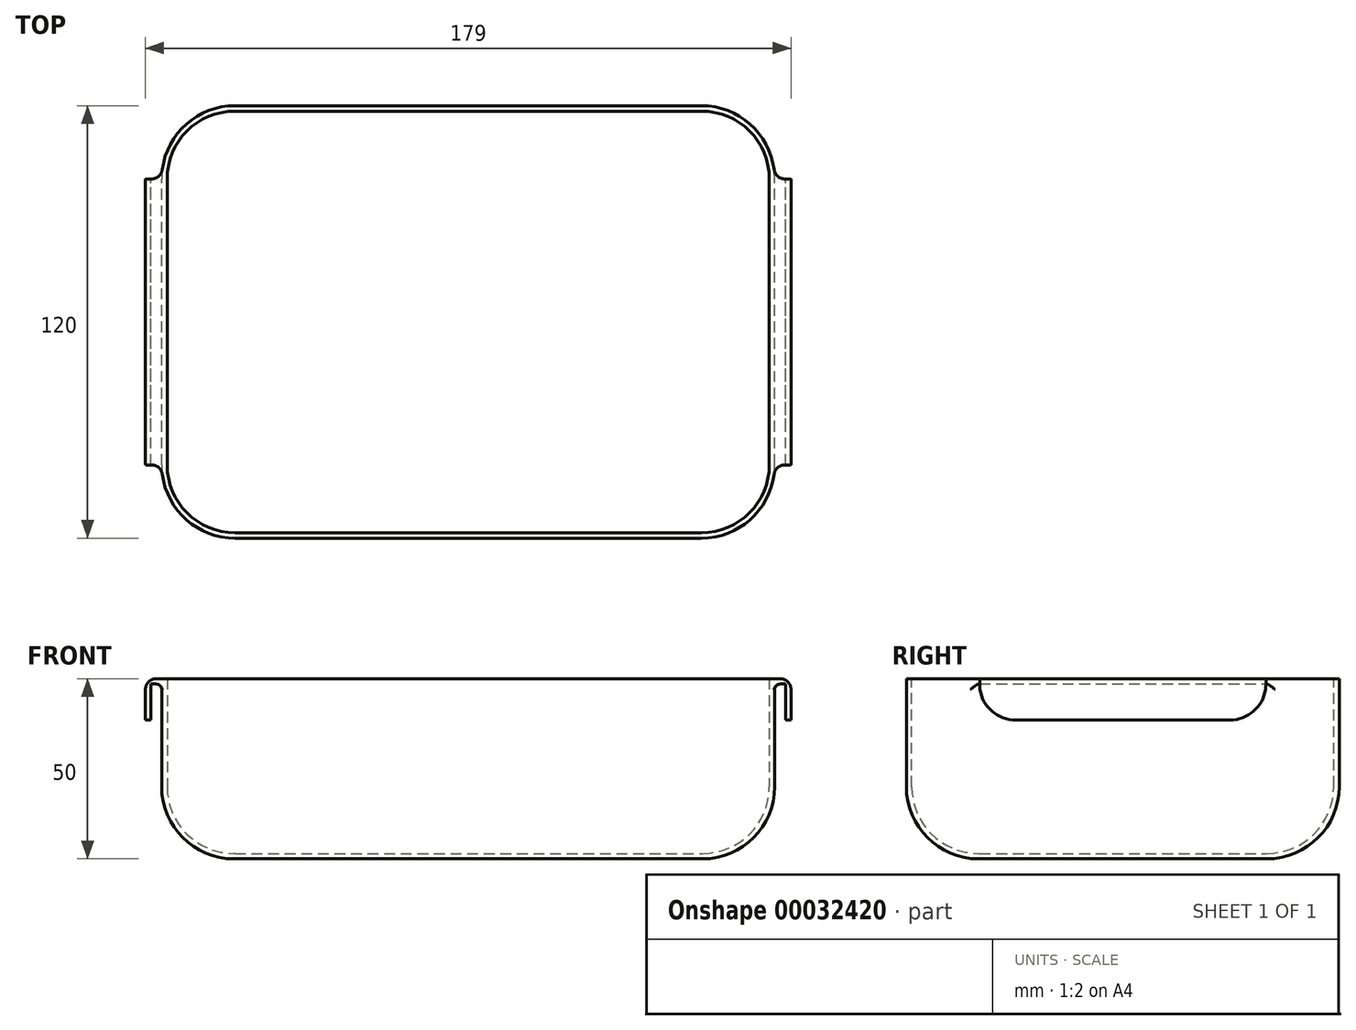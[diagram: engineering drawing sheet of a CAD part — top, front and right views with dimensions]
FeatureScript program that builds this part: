
annotation { "Feature Type Name" : "Feature", "Feature Type Description" : "" }
export const myFeature = defineFeature(function(context is Context, id is Id, definition is map)
    precondition{}
    {
        {
            var Q0;
            Q0=qCreatedBy(makeId("Top.planeOp"),FACE);
            var sketch = newSketch(context, id + "F0", { "sketchPlane" : qUnion([Q0])});
            skLineSegment(sketch, "E0.bottom", {"start": v(20.32, 0) * mm, "end": v(149.68, 0) * mm});
            skLineSegment(sketch, "E0.top", {"start": v(20.32, 120) * mm, "end": v(149.68, 120) * mm});
            skLineSegment(sketch, "E0.left", {"start": v(0, 20.32) * mm, "end": v(0, 99.68) * mm});
            skLineSegment(sketch, "E0.right", {"start": v(170, 20.32) * mm, "end": v(170, 99.68) * mm});
            skPoint(sketch, "E1.visualSharp", {"position": v(0, 120) * mm});
            skArc(sketch, "E1.filletArc", {"start": v(20.32, 120) * mm, "mid": v(5.95, 114.05) * mm, "end": v(0, 99.68) * mm});
            skPoint(sketch, "E2.visualSharp", {"position": v(170, 120) * mm});
            skArc(sketch, "E2.filletArc", {"start": v(170, 99.68) * mm, "mid": v(164.05, 114.05) * mm, "end": v(149.68, 120) * mm});
            skPoint(sketch, "E3.visualSharp", {"position": v(170, 0) * mm});
            skArc(sketch, "E3.filletArc", {"start": v(149.68, 0) * mm, "mid": v(164.05, 5.95) * mm, "end": v(170, 20.32) * mm});
            skPoint(sketch, "E4.visualSharp", {"position": v(0, 0) * mm});
            skArc(sketch, "E4.filletArc", {"start": v(0, 20.32) * mm, "mid": v(5.95, 5.95) * mm, "end": v(20.32, 0) * mm});
            skSolve(sketch);
        }
        {
            var Q0;
            Q0=makeQuery(id+"F0.imprint","IMPRINT",FACE,{"disambiguationData":[TD([[makeQuery(id+"F0.imprint","IMPRINT",EDGE,{"derivedFrom":sQuery(id+"F0.wireOp",EDGE,"E0.bottom")}),1.0]])]});
            extrude(context, id + "F1", {"entities" : qUnion([Q0]), "depth" : 50 * mm});
        }
        {
            var Q0;
            Q0=makeQuery(id+"F1.opExtrude","CAP_FACE",FACE,{"disambiguationData":[OSD([sQuery(id+"F0.wireOp",EDGE,"E0.bottom"),sQuery(id+"F0.wireOp",EDGE,"E0.top"),sQuery(id+"F0.wireOp",EDGE,"E0.left"),sQuery(id+"F0.wireOp",EDGE,"E0.right"),sQuery(id+"F0.wireOp",EDGE,"E1.filletArc"),sQuery(id+"F0.wireOp",EDGE,"E2.filletArc"),sQuery(id+"F0.wireOp",EDGE,"E3.filletArc"),sQuery(id+"F0.wireOp",EDGE,"E4.filletArc")])],"isStart":true});
            fillet(context, id + "F2", {"entities" : qUnion([Q0]), "radius" : 20 * mm, "tangentPropagation" : true, "allowEdgeOverflow" : false});
        }
        {
            var Q0;
            Q0=makeQuery(id+"F1.opExtrude","CAP_FACE",FACE,{"disambiguationData":[OSD([sQuery(id+"F0.wireOp",EDGE,"E0.bottom"),sQuery(id+"F0.wireOp",EDGE,"E0.top"),sQuery(id+"F0.wireOp",EDGE,"E0.left"),sQuery(id+"F0.wireOp",EDGE,"E0.right"),sQuery(id+"F0.wireOp",EDGE,"E1.filletArc"),sQuery(id+"F0.wireOp",EDGE,"E2.filletArc"),sQuery(id+"F0.wireOp",EDGE,"E3.filletArc"),sQuery(id+"F0.wireOp",EDGE,"E4.filletArc")])],"isStart":false});
            var sketch = newSketch(context, id + "F3", { "sketchPlane" : qUnion([Q0])});
            skLineSegment(sketch, "E5.bottom", {"start": v(0, 99.68) * mm, "end": v(-4.5, 99.68) * mm});
            skLineSegment(sketch, "E5.top", {"start": v(0, 20.32) * mm, "end": v(-4.5, 20.32) * mm});
            skLineSegment(sketch, "E5.right", {"start": v(-4.5, 99.68) * mm, "end": v(-4.5, 20.32) * mm});
            skLineSegment(sketch, "E6.bottom", {"start": v(170, 99.68) * mm, "end": v(174.5, 99.68) * mm});
            skLineSegment(sketch, "E6.top", {"start": v(170, 20.32) * mm, "end": v(174.5, 20.32) * mm});
            skLineSegment(sketch, "E6.right", {"start": v(174.5, 99.68) * mm, "end": v(174.5, 20.32) * mm});
            skArc(sketch, "E7.0", {"start": v(20.32, 120) * mm, "mid": v(5.95, 114.05) * mm, "end": v(0, 99.68) * mm});
            skLineSegment(sketch, "E7.1", {"start": v(20.32, 120) * mm, "end": v(149.68, 120) * mm});
            skArc(sketch, "E7.2", {"start": v(170, 99.68) * mm, "mid": v(164.05, 114.05) * mm, "end": v(149.68, 120) * mm});
            skArc(sketch, "E7.3", {"start": v(149.68, 0) * mm, "mid": v(164.05, 5.95) * mm, "end": v(170, 20.32) * mm});
            skLineSegment(sketch, "E7.4", {"start": v(20.32, 0) * mm, "end": v(149.68, 0) * mm});
            skArc(sketch, "E7.5", {"start": v(0, 20.32) * mm, "mid": v(5.95, 5.95) * mm, "end": v(20.32, 0) * mm});
            skSolve(sketch);
        }
        {
            var Q0;
            Q0 = qSketchRegion(id + "F3", true);
            extrude(context, id + "F4", {"entities" : qUnion([Q0]), "operationType" : NewBodyOperationType.ADD, "oppositeDirection" : true, "depth" : 1.5 * mm});
        }
        {
            var Q0;
            Q0=makeQuery(id+"F4.boolean.opBoolean","MERGE",FACE,{"derivedFrom":[makeQuery(id+"F1.opExtrude","CAP_FACE",FACE,{"disambiguationData":[OSD([sQuery(id+"F0.wireOp",EDGE,"E0.bottom"),sQuery(id+"F0.wireOp",EDGE,"E0.top"),sQuery(id+"F0.wireOp",EDGE,"E0.left"),sQuery(id+"F0.wireOp",EDGE,"E0.right"),sQuery(id+"F0.wireOp",EDGE,"E1.filletArc"),sQuery(id+"F0.wireOp",EDGE,"E2.filletArc"),sQuery(id+"F0.wireOp",EDGE,"E3.filletArc"),sQuery(id+"F0.wireOp",EDGE,"E4.filletArc")])],"isStart":false}),makeQuery(id+"F4.opExtrude","CAP_FACE",FACE,{"disambiguationData":[OSD([sQuery(id+"F3.wireOp",EDGE,"E5.bottom"),sQuery(id+"F3.wireOp",EDGE,"E5.top"),sQuery(id+"F3.wireOp",EDGE,"E5.right"),sQuery(id+"F3.wireOp",EDGE,"E6.bottom"),sQuery(id+"F3.wireOp",EDGE,"E6.top"),sQuery(id+"F3.wireOp",EDGE,"E6.right"),sQuery(id+"F3.wireOp",EDGE,"E7.0"),sQuery(id+"F3.wireOp",EDGE,"E7.1"),sQuery(id+"F3.wireOp",EDGE,"E7.2"),sQuery(id+"F3.wireOp",EDGE,"E7.3"),sQuery(id+"F3.wireOp",EDGE,"E7.4"),sQuery(id+"F3.wireOp",EDGE,"E7.5")])],"isStart":true})]});
            shell(context, id + "F5", {"entities" : qUnion([Q0]), "thickness" : 1.5 * mm});
        }
        {
            var Q0;
            {var subQ0=sQuery(id+"F3.wireOp",EDGE,"E6.bottom");var subQ1=sQuery(id+"F3.wireOp",EDGE,"E6.top");var subQ2=sQuery(id+"F3.wireOp",EDGE,"E6.right");Q0=makeQuery(id+"F4.boolean.opBoolean","SPLIT",FACE,{"disambiguationData":[TD([makeQuery(id+"F1.opExtrude","SWEPT_FACE",FACE,{"disambiguationData":[OSD([sQuery(id+"F0.wireOp",EDGE,"E0.right")])]})])],"derivedFrom":makeQuery(id+"F4.opExtrude","CAP_FACE",FACE,{"disambiguationData":[OSD([sQuery(id+"F3.wireOp",EDGE,"E5.bottom"),sQuery(id+"F3.wireOp",EDGE,"E5.top"),sQuery(id+"F3.wireOp",EDGE,"E5.right"),subQ0,subQ1,subQ2,sQuery(id+"F3.wireOp",EDGE,"E7.0"),sQuery(id+"F3.wireOp",EDGE,"E7.1"),sQuery(id+"F3.wireOp",EDGE,"E7.2"),sQuery(id+"F3.wireOp",EDGE,"E7.3"),sQuery(id+"F3.wireOp",EDGE,"E7.4"),sQuery(id+"F3.wireOp",EDGE,"E7.5")])],"isStart":false})});}
            var sketch = newSketch(context, id + "F6", { "sketchPlane" : qUnion([Q0])});
            skLineSegment(sketch, "E8.bottom", {"start": v(174.5, -20.32) * mm, "end": v(173, -20.32) * mm});
            skLineSegment(sketch, "E8.top", {"start": v(174.5, -99.68) * mm, "end": v(173, -99.68) * mm});
            skLineSegment(sketch, "E8.left", {"start": v(174.5, -20.32) * mm, "end": v(174.5, -99.68) * mm});
            skLineSegment(sketch, "E8.right", {"start": v(173, -20.32) * mm, "end": v(173, -99.68) * mm});
            skSolve(sketch);
        }
        {
            var Q0;
            Q0 = qSketchRegion(id + "F6", true);
            extrude(context, id + "F7", {"entities" : qUnion([Q0]), "operationType" : NewBodyOperationType.ADD, "depth" : 10 * mm});
        }
        {
            var Q0;
            {var subQ0=sQuery(id+"F3.wireOp",EDGE,"E5.bottom");var subQ1=sQuery(id+"F3.wireOp",EDGE,"E5.top");var subQ2=sQuery(id+"F3.wireOp",EDGE,"E5.right");Q0=makeQuery(id+"F4.boolean.opBoolean","SPLIT",FACE,{"disambiguationData":[TD([makeQuery(id+"F1.opExtrude","SWEPT_FACE",FACE,{"disambiguationData":[OSD([sQuery(id+"F0.wireOp",EDGE,"E0.left")])]})])],"derivedFrom":makeQuery(id+"F4.opExtrude","CAP_FACE",FACE,{"disambiguationData":[OSD([subQ0,subQ1,subQ2,sQuery(id+"F3.wireOp",EDGE,"E6.bottom"),sQuery(id+"F3.wireOp",EDGE,"E6.top"),sQuery(id+"F3.wireOp",EDGE,"E6.right"),sQuery(id+"F3.wireOp",EDGE,"E7.0"),sQuery(id+"F3.wireOp",EDGE,"E7.1"),sQuery(id+"F3.wireOp",EDGE,"E7.2"),sQuery(id+"F3.wireOp",EDGE,"E7.3"),sQuery(id+"F3.wireOp",EDGE,"E7.4"),sQuery(id+"F3.wireOp",EDGE,"E7.5")])],"isStart":false})});}
            var sketch = newSketch(context, id + "F8", { "sketchPlane" : qUnion([Q0])});
            skLineSegment(sketch, "E9.bottom", {"start": v(-4.5, -20.32) * mm, "end": v(-3, -20.32) * mm});
            skLineSegment(sketch, "E9.top", {"start": v(-4.5, -99.68) * mm, "end": v(-3, -99.68) * mm});
            skLineSegment(sketch, "E9.left", {"start": v(-4.5, -20.32) * mm, "end": v(-4.5, -99.68) * mm});
            skLineSegment(sketch, "E9.right", {"start": v(-3, -20.32) * mm, "end": v(-3, -99.68) * mm});
            skSolve(sketch);
        }
        {
            var Q0;
            Q0 = qSketchRegion(id + "F8", true);
            extrude(context, id + "F9", {"entities" : qUnion([Q0]), "operationType" : NewBodyOperationType.ADD, "depth" : 10 * mm});
        }
        {
            var Q0;
            {var subQ0=sQuery(id+"F0.wireOp",EDGE,"E0.right");Q0=makeQuery(id+"F4.boolean.opBoolean","MERGE",EDGE,{"derivedFrom":[makeQuery(id+"F1.opExtrude","SWEPT_EDGE",EDGE,{"disambiguationData":[OSD([subQ0,sQuery(id+"F0.wireOp",EDGE,"E3.filletArc")])]}),makeQuery(id+"F4.opExtrude","SWEPT_EDGE",EDGE,{"disambiguationData":[OSD([subQ0,sQuery(id+"F3.wireOp",EDGE,"E6.top"),sQuery(id+"F3.wireOp",EDGE,"E7.3")])]})]});}
            var Q1;
            {var subQ0=sQuery(id+"F0.wireOp",EDGE,"E0.right");Q1=makeQuery(id+"F4.boolean.opBoolean","MERGE",EDGE,{"derivedFrom":[makeQuery(id+"F1.opExtrude","SWEPT_EDGE",EDGE,{"disambiguationData":[OSD([subQ0,sQuery(id+"F0.wireOp",EDGE,"E2.filletArc")])]}),makeQuery(id+"F4.opExtrude","SWEPT_EDGE",EDGE,{"disambiguationData":[OSD([subQ0,sQuery(id+"F3.wireOp",EDGE,"E6.bottom"),sQuery(id+"F3.wireOp",EDGE,"E7.2")])]})]});}
            var Q2;
            {var subQ0=sQuery(id+"F0.wireOp",EDGE,"E0.left");Q2=makeQuery(id+"F4.boolean.opBoolean","MERGE",EDGE,{"derivedFrom":[makeQuery(id+"F1.opExtrude","SWEPT_EDGE",EDGE,{"disambiguationData":[OSD([subQ0,sQuery(id+"F0.wireOp",EDGE,"E1.filletArc")])]}),makeQuery(id+"F4.opExtrude","SWEPT_EDGE",EDGE,{"disambiguationData":[OSD([subQ0,sQuery(id+"F3.wireOp",EDGE,"E5.bottom"),sQuery(id+"F3.wireOp",EDGE,"E7.0")])]})]});}
            var Q3;
            {var subQ0=sQuery(id+"F0.wireOp",EDGE,"E0.left");Q3=makeQuery(id+"F4.boolean.opBoolean","MERGE",EDGE,{"derivedFrom":[makeQuery(id+"F1.opExtrude","SWEPT_EDGE",EDGE,{"disambiguationData":[OSD([subQ0,sQuery(id+"F0.wireOp",EDGE,"E4.filletArc")])]}),makeQuery(id+"F4.opExtrude","SWEPT_EDGE",EDGE,{"disambiguationData":[OSD([subQ0,sQuery(id+"F3.wireOp",EDGE,"E5.top"),sQuery(id+"F3.wireOp",EDGE,"E7.5")])]})]});}
            fillet(context, id + "F10", {"entities" : qUnion([Q0, Q1, Q2, Q3]), "radius" : 2.96 * mm, "tangentPropagation" : true, "allowEdgeOverflow" : false});
        }
        {
            var Q0;
            Q0=makeQuery(id+"F9.opExtrude","CAP_EDGE",EDGE,{"disambiguationData":[OSD([sQuery(id+"F8.wireOp",EDGE,"E9.right")])],"isStart":true});
            var Q1;
            Q1=makeQuery(id+"F4.boolean.opBoolean","INTERSECT",EDGE,{"derivedFrom":[makeQuery(id+"F1.opExtrude","SWEPT_FACE",FACE,{"disambiguationData":[OSD([sQuery(id+"F0.wireOp",EDGE,"E0.left")])]}),makeQuery(id+"F4.opExtrude","CAP_FACE",FACE,{"disambiguationData":[OSD([sQuery(id+"F3.wireOp",EDGE,"E5.bottom"),sQuery(id+"F3.wireOp",EDGE,"E5.top"),sQuery(id+"F3.wireOp",EDGE,"E5.right"),sQuery(id+"F3.wireOp",EDGE,"E6.bottom"),sQuery(id+"F3.wireOp",EDGE,"E6.top"),sQuery(id+"F3.wireOp",EDGE,"E6.right"),sQuery(id+"F3.wireOp",EDGE,"E7.0"),sQuery(id+"F3.wireOp",EDGE,"E7.1"),sQuery(id+"F3.wireOp",EDGE,"E7.2"),sQuery(id+"F3.wireOp",EDGE,"E7.3"),sQuery(id+"F3.wireOp",EDGE,"E7.4"),sQuery(id+"F3.wireOp",EDGE,"E7.5")])],"isStart":false})]});
            var Q2;
            Q2=makeQuery(id+"F4.boolean.opBoolean","INTERSECT",EDGE,{"derivedFrom":[makeQuery(id+"F1.opExtrude","SWEPT_FACE",FACE,{"disambiguationData":[OSD([sQuery(id+"F0.wireOp",EDGE,"E0.right")])]}),makeQuery(id+"F4.opExtrude","CAP_FACE",FACE,{"disambiguationData":[OSD([sQuery(id+"F3.wireOp",EDGE,"E5.bottom"),sQuery(id+"F3.wireOp",EDGE,"E5.top"),sQuery(id+"F3.wireOp",EDGE,"E5.right"),sQuery(id+"F3.wireOp",EDGE,"E6.bottom"),sQuery(id+"F3.wireOp",EDGE,"E6.top"),sQuery(id+"F3.wireOp",EDGE,"E6.right"),sQuery(id+"F3.wireOp",EDGE,"E7.0"),sQuery(id+"F3.wireOp",EDGE,"E7.1"),sQuery(id+"F3.wireOp",EDGE,"E7.2"),sQuery(id+"F3.wireOp",EDGE,"E7.3"),sQuery(id+"F3.wireOp",EDGE,"E7.4"),sQuery(id+"F3.wireOp",EDGE,"E7.5")])],"isStart":false})]});
            var Q3;
            Q3=makeQuery(id+"F7.opExtrude","CAP_EDGE",EDGE,{"disambiguationData":[OSD([sQuery(id+"F6.wireOp",EDGE,"E8.right")])],"isStart":true});
            fillet(context, id + "F11", {"entities" : qUnion([Q0, Q1, Q2, Q3]), "radius" : 1.5 * mm, "tangentPropagation" : true, "allowEdgeOverflow" : false});
        }
        {
            var Q0;
            Q0=makeQuery(id+"F4.opExtrude","CAP_EDGE",EDGE,{"disambiguationData":[OSD([sQuery(id+"F3.wireOp",EDGE,"E6.right")])],"isStart":true});
            var Q1;
            Q1=makeQuery(id+"F4.opExtrude","CAP_EDGE",EDGE,{"disambiguationData":[OSD([sQuery(id+"F3.wireOp",EDGE,"E5.right")])],"isStart":true});
            fillet(context, id + "F12", {"entities" : qUnion([Q0, Q1]), "radius" : 3 * mm, "tangentPropagation" : true, "allowEdgeOverflow" : false});
        }
        {
            var Q0;
            Q0=makeQuery(id+"F7.opExtrude","CAP_EDGE",EDGE,{"disambiguationData":[OSD([sQuery(id+"F6.wireOp",EDGE,"E8.bottom")])],"isStart":false});
            var Q1;
            Q1=makeQuery(id+"F7.opExtrude","CAP_EDGE",EDGE,{"disambiguationData":[OSD([sQuery(id+"F6.wireOp",EDGE,"E8.top")])],"isStart":false});
            var Q2;
            Q2=makeQuery(id+"F9.opExtrude","CAP_EDGE",EDGE,{"disambiguationData":[OSD([sQuery(id+"F8.wireOp",EDGE,"E9.bottom")])],"isStart":false});
            var Q3;
            Q3=makeQuery(id+"F9.opExtrude","CAP_EDGE",EDGE,{"disambiguationData":[OSD([sQuery(id+"F8.wireOp",EDGE,"E9.top")])],"isStart":false});
            fillet(context, id + "F13", {"entities" : qUnion([Q0, Q1, Q2, Q3]), "radius" : 9.94 * mm, "tangentPropagation" : true, "allowEdgeOverflow" : false});
        }
    });
